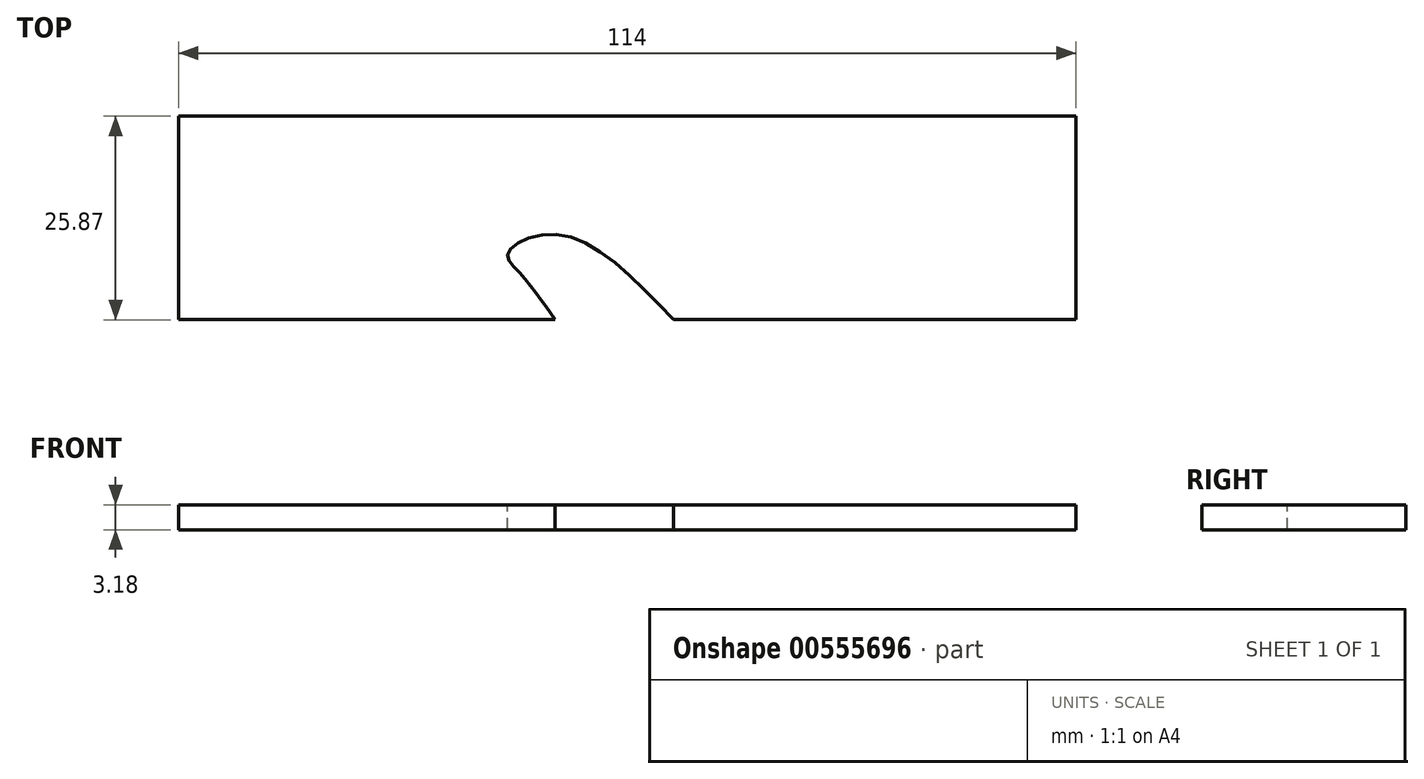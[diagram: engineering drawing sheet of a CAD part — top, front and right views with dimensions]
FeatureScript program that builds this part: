
annotation { "Feature Type Name" : "Feature", "Feature Type Description" : "" }
export const myFeature = defineFeature(function(context is Context, id is Id, definition is map)
    precondition{}
    {
        {
            var Q0;
            Q0=qCreatedBy(makeId("Top.planeOp"),FACE);
            var sketch = newSketch(context, id + "F0", { "sketchPlane" : qUnion([Q0])});
            skLineSegment(sketch, "E0.bottom", {"start": v(-84.07, -11.13) * mm, "end": v(29.93, -11.13) * mm});
            skLineSegment(sketch, "E0.top", {"start": v(-84.07, -37) * mm, "end": v(29.93, -37) * mm});
            skLineSegment(sketch, "E0.left", {"start": v(-84.07, -11.13) * mm, "end": v(-84.07, -37) * mm});
            skLineSegment(sketch, "E0.right", {"start": v(29.93, -11.13) * mm, "end": v(29.93, -37) * mm});
            skFitSpline(sketch, "E1", {"points": [v(-21.2, -37) * mm, v(-35.94, -26.17) * mm, v(-42.26, -28.58) * mm, v(-41.06, -30.68) * mm, v(-38.35, -33.99) * mm, v(-36.24, -37) * mm], "startDerivative": vector(-42.86, 45.18) * mm, "endDerivative": vector(13.02, -19.11) * mm});
            skSolve(sketch);
        }
        {
            var Q0;
            Q0=makeQuery(id+"F0.imprint","IMPRINT",FACE,{"disambiguationData":[TD([[makeQuery(id+"F0.imprint","IMPRINT",EDGE,{"derivedFrom":sQuery(id+"F0.wireOp",EDGE,"E0.bottom")}),-1.0]])]});
            extrude(context, id + "F1", {"entities" : qUnion([Q0]), "depth" : 3.17 * mm, "offsetDistance" : 25.4 * mm});
        }
    });
